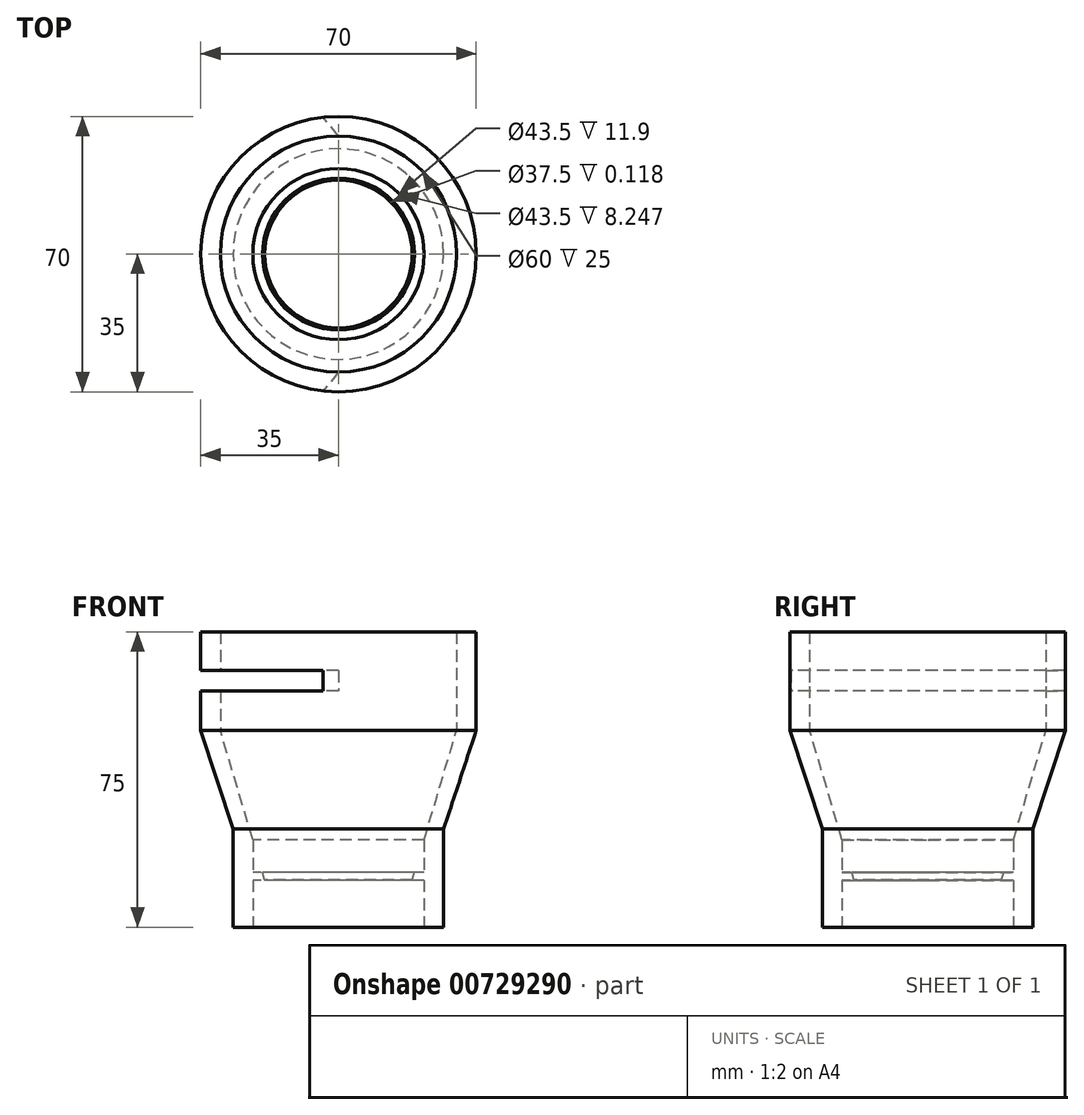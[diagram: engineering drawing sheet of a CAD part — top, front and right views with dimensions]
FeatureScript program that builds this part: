
annotation { "Feature Type Name" : "Feature", "Feature Type Description" : "" }
export const myFeature = defineFeature(function(context is Context, id is Id, definition is map)
    precondition{}
    {
        {
            var Q0;
            Q0=qCreatedBy(makeId("Top.planeOp"),FACE);
            var sketch = newSketch(context, id + "F0", { "sketchPlane" : qUnion([Q0])});
            skCircle(sketch, "E0", {"center": v(0, 0) * mm, "radius": 26.75 * mm});
            skCircle(sketch, "E1", {"center": v(0, 0) * mm, "radius": 21.75 * mm});
            skSolve(sketch);
        }
        {
            var Q0;
            Q0 = qSketchRegion(id + "F0", true);
            extrude(context, id + "F1", {"entities" : qUnion([Q0]), "depth" : 25 * mm, "offsetDistance" : 25 * mm});
        }
        {
            var Q0;
            Q0=qCreatedBy(makeId("Top.planeOp"),FACE);
            cPlane(context, id + "F2", {"entities" : qUnion([Q0]), "cplaneType" : CPlaneType.OFFSET, "offset" : 11.9 * mm, "width" : 150 * mm, "height" : 150 * mm});
        }
        {
            var Q0;
            Q0=qCreatedBy(id+"F2.planeOp",FACE);
            var sketch = newSketch(context, id + "F3", { "sketchPlane" : qUnion([Q0])});
            skCircle(sketch, "E2", {"center": v(0, 0) * mm, "radius": 18.75 * mm});
            skCircle(sketch, "E3", {"center": v(0, 0) * mm, "radius": 22.94 * mm});
            skSolve(sketch);
        }
        {
            var Q0;
            Q0 = qSketchRegion(id + "F3", true);
            extrude(context, id + "F4", {"entities" : qUnion([Q0]), "operationType" : NewBodyOperationType.ADD, "depth" : 2 * mm, "offsetDistance" : 25 * mm});
        }
        {
            var Q0;
            Q0=makeQuery(id+"F1.opExtrude","CAP_FACE",FACE,{"disambiguationData":[OSD([sQuery(id+"F0.wireOp",EDGE,"E0"),sQuery(id+"F0.wireOp",EDGE,"E1")])],"isStart":false});
            cPlane(context, id + "F5", {"entities" : qUnion([Q0]), "cplaneType" : CPlaneType.OFFSET, "offset" : 25 * mm, "width" : 150 * mm, "height" : 150 * mm});
        }
        {
            var Q0;
            Q0=qCreatedBy(id+"F5.planeOp",FACE);
            var sketch = newSketch(context, id + "F6", { "sketchPlane" : qUnion([Q0])});
            skCircle(sketch, "E4", {"center": v(0, 0) * mm, "radius": 35 * mm});
            skSolve(sketch);
        }
        {
            var Q0;
            Q0=makeQuery(id+"F1.opExtrude","CAP_FACE",FACE,{"disambiguationData":[OSD([sQuery(id+"F0.wireOp",EDGE,"E0"),sQuery(id+"F0.wireOp",EDGE,"E1")])],"isStart":false});
            var sketch = newSketch(context, id + "F7", { "sketchPlane" : qUnion([Q0])});
            skCircle(sketch, "E5", {"center": v(0, 0) * mm, "radius": 26.75 * mm});
            skSolve(sketch);
        }
        {
            var Q1;
            Q1 = qSketchRegion(id + "F6", true);
            var Q2;
            Q2 = qSketchRegion(id + "F7", true);
            loft(context, id + "F8", {"operationType" : NewBodyOperationType.ADD, "sheetProfilesArray" : [{ "sheetProfileEntities" : qUnion([Q1]) }, { "sheetProfileEntities" : qUnion([Q2]) }]});
        }
        {
            var Q0;
            Q0=makeQuery(id+"F8.opLoft","CAP_FACE",FACE,{"disambiguationData":[OSD([makeQuery(id+"F6.imprint","IMPRINT",FACE,{"disambiguationData":[TD([[makeQuery(id+"F6.imprint","IMPRINT",EDGE,{"derivedFrom":sQuery(id+"F6.wireOp",EDGE,"E4")}),1.0]])]})])],"isStart":true});
            var sketch = newSketch(context, id + "F9", { "sketchPlane" : qUnion([Q0])});
            skCircle(sketch, "E6", {"center": v(0, 0) * mm, "radius": 30 * mm});
            skSolve(sketch);
        }
        {
            var Q0;
            Q0=makeQuery(id+"F4.opExtrude","CAP_FACE",FACE,{"disambiguationData":[OSD([sQuery(id+"F3.wireOp",EDGE,"E2"),sQuery(id+"F3.wireOp",EDGE,"E3")])],"isStart":true});
            var sketch = newSketch(context, id + "F10", { "sketchPlane" : qUnion([Q0])});
            skCircle(sketch, "E7", {"center": v(0, 0) * mm, "radius": 18.71 * mm});
            skSolve(sketch);
        }
        {
            var Q1;
            Q1 = qSketchRegion(id + "F9", true);
            var Q2;
            Q2 = qSketchRegion(id + "F10", true);
            loft(context, id + "F11", {"operationType" : NewBodyOperationType.REMOVE, "sheetProfilesArray" : [{ "sheetProfileEntities" : qUnion([Q1]) }, { "sheetProfileEntities" : qUnion([Q2]) }]});
        }
        {
            var Q0;
            Q0=makeQuery(id+"F8.opLoft","CAP_FACE",FACE,{"disambiguationData":[OSD([makeQuery(id+"F6.imprint","IMPRINT",FACE,{"disambiguationData":[TD([[makeQuery(id+"F6.imprint","IMPRINT",EDGE,{"derivedFrom":sQuery(id+"F6.wireOp",EDGE,"E4")}),1.0]])]})])],"isStart":true});
            var sketch = newSketch(context, id + "F12", { "sketchPlane" : qUnion([Q0])});
            skCircle(sketch, "E8", {"center": v(0, 0) * mm, "radius": 35 * mm});
            skCircle(sketch, "E9", {"center": v(0, 0) * mm, "radius": 30 * mm});
            skSolve(sketch);
        }
        {
            var Q0;
            Q0 = qSketchRegion(id + "F12", true);
            extrude(context, id + "F13", {"entities" : qUnion([Q0]), "operationType" : NewBodyOperationType.ADD, "depth" : 25 * mm, "offsetDistance" : 25 * mm});
        }
        {
            var Q0;
            Q0=makeQuery(id+"F13.opExtrude","CAP_FACE",FACE,{"disambiguationData":[OSD([sQuery(id+"F12.wireOp",EDGE,"E8"),sQuery(id+"F12.wireOp",EDGE,"E9")])],"isStart":false});
            cPlane(context, id + "F14", {"entities" : qUnion([Q0]), "cplaneType" : CPlaneType.OFFSET, "offset" : 15 * mm, "oppositeDirection" : true, "width" : 150 * mm, "height" : 150 * mm});
        }
        {
            var Q0;
            Q0=qCreatedBy(id+"F14.planeOp",FACE);
            var sketch = newSketch(context, id + "F15", { "sketchPlane" : qUnion([Q0])});
            skArc(sketch, "E10", {"start": v(-3.9, 34.78) * mm, "mid": v(-35, 0) * mm, "end": v(-3.9, -34.78) * mm});
            skArc(sketch, "E11", {"start": v(-0.03, 30) * mm, "mid": v(-30, 0) * mm, "end": v(-0.03, -30) * mm});
            skLineSegment(sketch, "E12", {"start": v(-0.03, 30) * mm, "end": v(-0.03, -30) * mm});
            skLineSegment(sketch, "E13", {"start": v(-0.03, 30) * mm, "end": v(-3.9, 34.78) * mm});
            skLineSegment(sketch, "E14", {"start": v(-0.03, -30) * mm, "end": v(-3.9, -34.78) * mm});
            skSolve(sketch);
        }
        {
            var Q0;
            Q0 = qSketchRegion(id + "F15", true);
            extrude(context, id + "F16", {"entities" : qUnion([Q0]), "operationType" : NewBodyOperationType.REMOVE, "depth" : 5.2 * mm, "offsetDistance" : 25 * mm});
        }
    });
